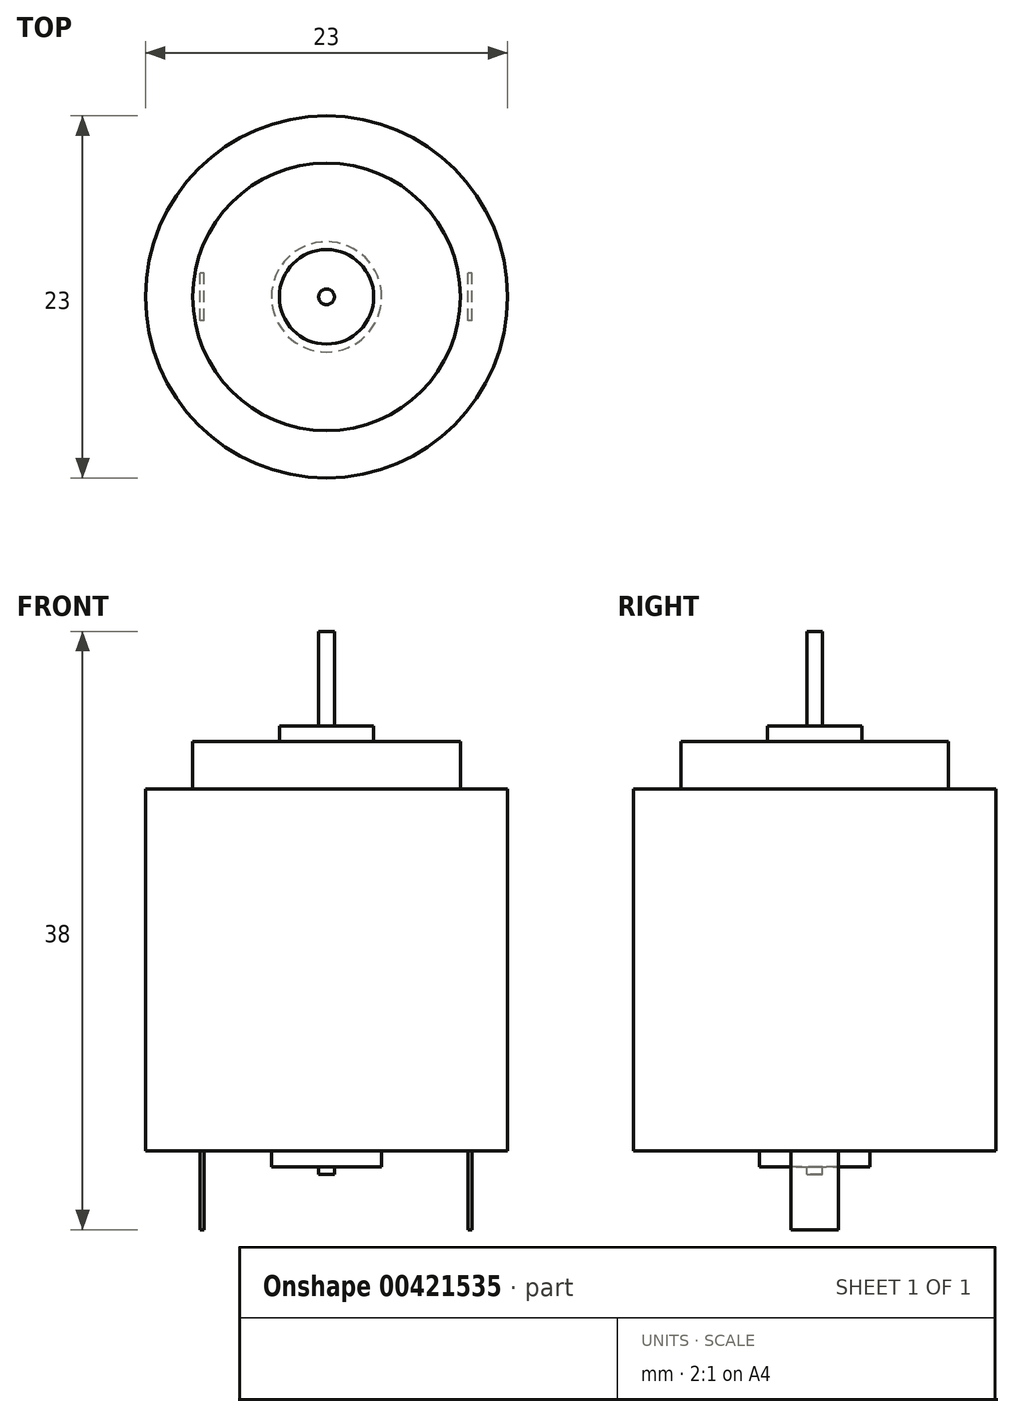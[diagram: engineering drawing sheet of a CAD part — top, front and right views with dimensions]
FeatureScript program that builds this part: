
annotation { "Feature Type Name" : "Feature", "Feature Type Description" : "" }
export const myFeature = defineFeature(function(context is Context, id is Id, definition is map)
    precondition{}
    {
        {
            var Q0;
            Q0=qCreatedBy(makeId("Top.planeOp"),FACE);
            var sketch = newSketch(context, id + "F0", { "sketchPlane" : qUnion([Q0])});
            skCircle(sketch, "E0", {"center": v(0, 0) * mm, "radius": 11.5 * mm});
            skSolve(sketch);
        }
        {
            var Q0;
            Q0 = qSketchRegion(id + "F0", true);
            extrude(context, id + "F1", {"entities" : qUnion([Q0]), "depth" : 23 * mm});
        }
        {
            var Q0;
            Q0=makeQuery(id+"F1.opExtrude","CAP_FACE",FACE,{"disambiguationData":[OSD([sQuery(id+"F0.wireOp",EDGE,"E0")])],"isStart":false});
            var sketch = newSketch(context, id + "F2", { "sketchPlane" : qUnion([Q0])});
            skCircle(sketch, "E1", {"center": v(0, 0) * mm, "radius": 8.5 * mm});
            skSolve(sketch);
        }
        {
            var Q0;
            Q0 = qSketchRegion(id + "F2", true);
            extrude(context, id + "F3", {"entities" : qUnion([Q0]), "depth" : 3 * mm});
        }
        {
            var Q0;
            Q0=makeQuery(id+"F3.opExtrude","CAP_FACE",FACE,{"disambiguationData":[OSD([sQuery(id+"F2.wireOp",EDGE,"E1")])],"isStart":false});
            var sketch = newSketch(context, id + "F4", { "sketchPlane" : qUnion([Q0])});
            skCircle(sketch, "E2", {"center": v(0, 0) * mm, "radius": 3 * mm});
            skSolve(sketch);
        }
        {
            var Q0;
            Q0 = qSketchRegion(id + "F4", true);
            extrude(context, id + "F5", {"entities" : qUnion([Q0]), "operationType" : NewBodyOperationType.ADD, "depth" : 1 * mm});
        }
        {
            var Q0;
            Q0=makeQuery(id+"F5.opExtrude","CAP_FACE",FACE,{"disambiguationData":[OSD([sQuery(id+"F4.wireOp",EDGE,"E2")])],"isStart":false});
            var sketch = newSketch(context, id + "F6", { "sketchPlane" : qUnion([Q0])});
            skCircle(sketch, "E3", {"center": v(0, 0) * mm, "radius": 0.5 * mm});
            skSolve(sketch);
        }
        {
            var Q0;
            Q0 = qSketchRegion(id + "F6", true);
            extrude(context, id + "F7", {"entities" : qUnion([Q0]), "operationType" : NewBodyOperationType.ADD, "depth" : 6 * mm});
        }
        {
            var Q0;
            Q0=makeQuery(id+"F1.opExtrude","CAP_FACE",FACE,{"disambiguationData":[OSD([sQuery(id+"F0.wireOp",EDGE,"E0")])],"isStart":true});
            var sketch = newSketch(context, id + "F8", { "sketchPlane" : qUnion([Q0])});
            skCircle(sketch, "E4", {"center": v(0, 0) * mm, "radius": 3.5 * mm});
            skSolve(sketch);
        }
        {
            var Q0;
            Q0 = qSketchRegion(id + "F8", true);
            extrude(context, id + "F9", {"entities" : qUnion([Q0]), "operationType" : NewBodyOperationType.ADD, "depth" : 1 * mm});
        }
        {
            var Q0;
            Q0=makeQuery(id+"F9.opExtrude","CAP_FACE",FACE,{"disambiguationData":[OSD([sQuery(id+"F8.wireOp",EDGE,"E4")])],"isStart":false});
            var sketch = newSketch(context, id + "F10", { "sketchPlane" : qUnion([Q0])});
            skCircle(sketch, "E5", {"center": v(0, 0) * mm, "radius": 0.5 * mm});
            skSolve(sketch);
        }
        {
            var Q0;
            Q0 = qSketchRegion(id + "F10", true);
            extrude(context, id + "F11", {"entities" : qUnion([Q0]), "operationType" : NewBodyOperationType.ADD, "depth" : 0.5 * mm});
        }
        {
            var Q0;
            Q0=makeQuery(id+"F1.opExtrude","CAP_FACE",FACE,{"disambiguationData":[OSD([sQuery(id+"F0.wireOp",EDGE,"E0")])],"isStart":true});
            var sketch = newSketch(context, id + "F12", { "sketchPlane" : qUnion([Q0])});
            skLineSegment(sketch, "E6", {"start": v(-10.9, 0) * mm, "end": v(10.9, 0) * mm, "construction": true});
            skPoint(sketch, "E7", {"position": v(-7.9, 0) * mm});
            skPoint(sketch, "E8", {"position": v(9.1, 0) * mm});
            skLineSegment(sketch, "E9.bottom", {"start": v(-7.78, 1.5) * mm, "end": v(-8.03, 1.5) * mm});
            skLineSegment(sketch, "E9.top", {"start": v(-7.78, -1.5) * mm, "end": v(-8.03, -1.5) * mm});
            skLineSegment(sketch, "E9.left", {"start": v(-7.78, 1.5) * mm, "end": v(-7.78, -1.5) * mm});
            skLineSegment(sketch, "E9.right", {"start": v(-8.03, 1.5) * mm, "end": v(-8.03, -1.5) * mm});
            skLineSegment(sketch, "E10.bottom", {"start": v(9.23, 1.5) * mm, "end": v(8.98, 1.5) * mm});
            skLineSegment(sketch, "E10.top", {"start": v(9.23, -1.5) * mm, "end": v(8.98, -1.5) * mm});
            skLineSegment(sketch, "E10.left", {"start": v(9.23, 1.5) * mm, "end": v(9.23, -1.5) * mm});
            skLineSegment(sketch, "E10.right", {"start": v(8.98, 1.5) * mm, "end": v(8.98, -1.5) * mm});
            skSolve(sketch);
        }
        {
            var Q0;
            Q0 = qSketchRegion(id + "F12", true);
            extrude(context, id + "F13", {"entities" : qUnion([Q0]), "operationType" : NewBodyOperationType.ADD, "depth" : 5 * mm});
        }
    });
